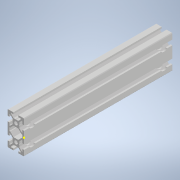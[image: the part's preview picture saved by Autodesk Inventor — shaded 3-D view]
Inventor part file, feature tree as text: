
AUTODESK INVENTOR PART (.ipt)
format: ipt  version: 2022 (Build 260153000, 153)  size: 439,296 bytes
history: native  units: mm
features: other x9, sketch x7, revolve x4, hole x3, extrude x1, pattern_linear x1
ambient origin geometry x8: Origin, YZ Plane, XZ Plane, XY Plane, X Axis, Y Axis, Z Axis, Center Point
bodies: Solid1 (feature_tree)
feature tree (25):
  extrude  "Extrusion1"  Depth=10.0mm TaperAngle=0.0deg
  hole  "Hole1"  [1 undecoded]
  pattern_linear  "Rectangular Pattern1"  Spacing1=360.0deg  [1 undecoded]
  revolve  "Revolution1"  [1 undecoded]
  revolve  "Revolution2"  [1 undecoded]
  revolve  "Revolution3"  [1 undecoded]
  revolve  "Revolution4"  [1 undecoded]
  other  "C1_XY"
  other  "C1_YZ"
  other  "C1_ZX"
  other  "C1_X"
  other  "C1_Y"
  other  "C1_Z"
  other  "C1_Center"
  sketch  "スケッチ8"
  hole  "穴2"  [1 undecoded]
  hole  "穴3"  [1 undecoded]
  sketch  "Sketch_1"  dims[d0=180.0mm d1=0.0mm]
  sketch  "Sketch2"  dims[d2=4.2mm d3=6.0mm d4=4.0mm d5=2.0mm d6=90.0deg d7=180.0mm d8=0.0mm d9=20.0mm d11=20.0mm d12=10.0mm d14=0.0mm]
  sketch  "Sketch_50"  dims[d15=360.0deg d16=360.0deg]
  other  "_p_______27_Sketch_50_0"
  sketch  "Sketch_51"  dims[d17=360.0deg d18=360.0deg d19=0.0mm d20=3.0mm d21=136.0mm d22=20.0mm d24=20.0mm d25=20.0mm d27=24.0mm d30=3.2mm d31=6.0mm d32=4.0mm d33=2.0mm d34=90.0deg d35=6.0mm d36=20.594885mm d37=6.0mm d38=6.0mm d39=4.0mm d40=2.0mm d41=90.0deg d42=3.0mm d43=20.594885mm]
  other  "_p_______28_Sketch_51_0"
  sketch  "スケッチ9"
  sketch  "スケッチ10"
note: 8 required parameter values undecoded (feature->parameter linkage not recoverable at this tier; creation-order binding heuristic only, values carry confidence <= 0.55)